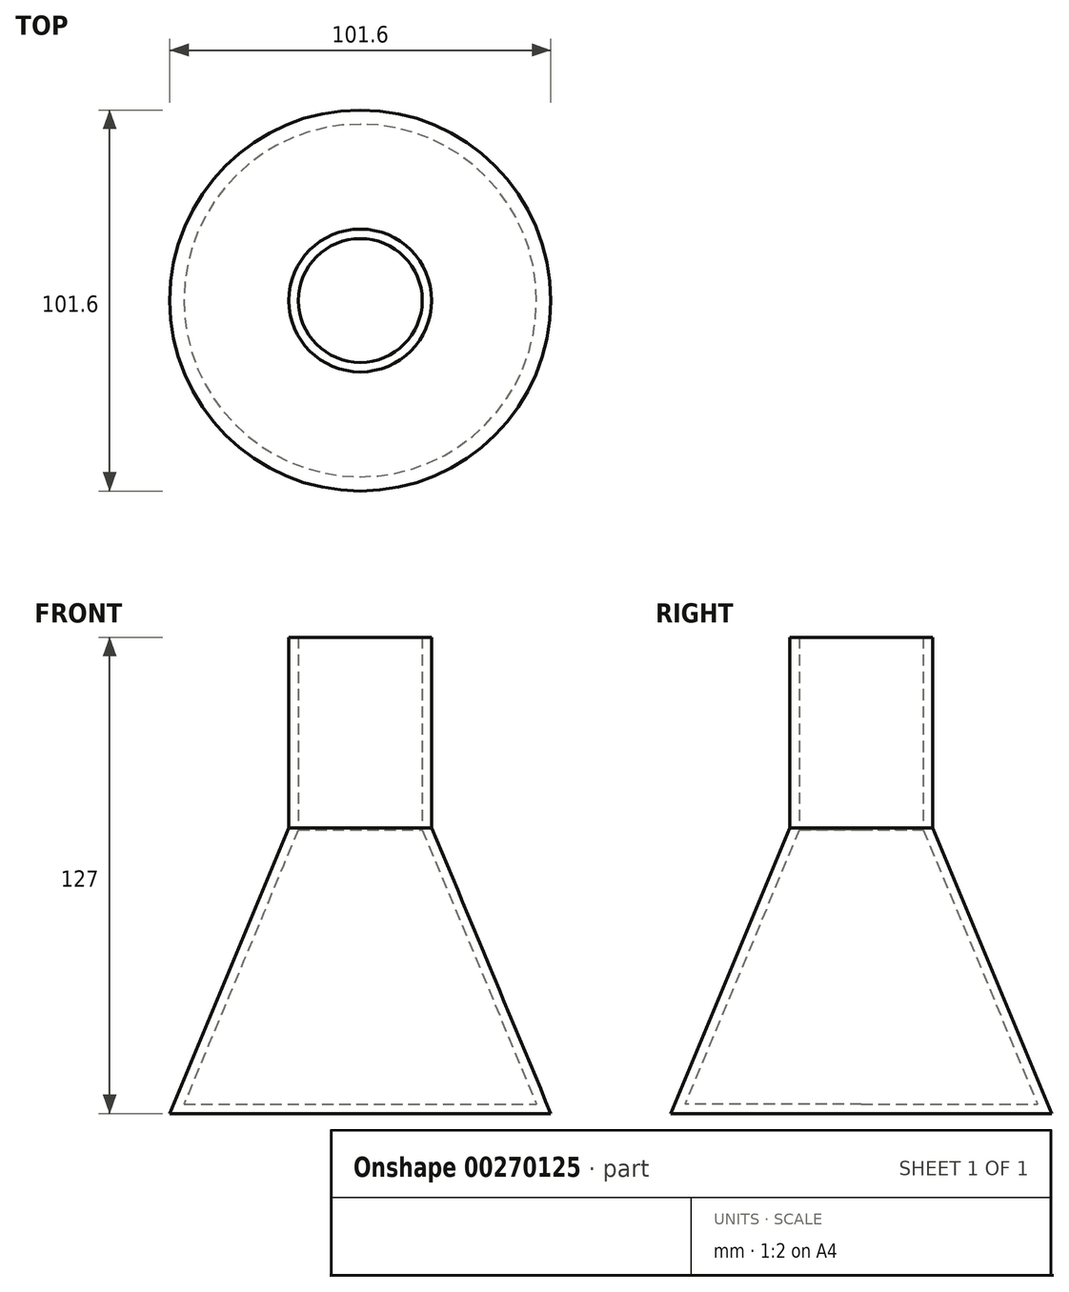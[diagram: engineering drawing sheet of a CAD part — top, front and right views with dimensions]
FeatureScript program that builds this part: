
annotation { "Feature Type Name" : "Feature", "Feature Type Description" : "" }
export const myFeature = defineFeature(function(context is Context, id is Id, definition is map)
    precondition{}
    {
        {
            var Q0;
            Q0=qCreatedBy(makeId("Top.planeOp"),FACE);
            var sketch = newSketch(context, id + "F0", { "sketchPlane" : qUnion([Q0])});
            skCircle(sketch, "E0", {"center": v(0, 0) * mm, "radius": 50.8 * mm});
            skSolve(sketch);
        }
        {
            var Q0;
            Q0=qCreatedBy(makeId("Top.planeOp"),FACE);
            cPlane(context, id + "F1", {"entities" : qUnion([Q0]), "cplaneType" : CPlaneType.OFFSET, "offset" : 76.2 * mm, "width" : 152.4 * mm, "height" : 152.4 * mm});
        }
        {
            var Q0;
            Q0=qCreatedBy(id+"F1.planeOp",FACE);
            var sketch = newSketch(context, id + "F2", { "sketchPlane" : qUnion([Q0])});
            skCircle(sketch, "E1", {"center": v(0, 0) * mm, "radius": 19.05 * mm});
            skSolve(sketch);
        }
        {
            var Q0;
            Q0=makeQuery(id+"F0.imprint","IMPRINT",FACE,{"disambiguationData":[TD([[makeQuery(id+"F0.imprint","IMPRINT",EDGE,{"derivedFrom":sQuery(id+"F0.wireOp",EDGE,"E0")}),1.0]])]});
            var Q1;
            Q1=makeQuery(id+"F2.imprint","IMPRINT",FACE,{"disambiguationData":[TD([[makeQuery(id+"F2.imprint","IMPRINT",EDGE,{"derivedFrom":sQuery(id+"F2.wireOp",EDGE,"E1")}),1.0]])]});
            loft(context, id + "F3", {"sheetProfilesArray" : [{ "sheetProfileEntities" : qUnion([Q0]) }, { "sheetProfileEntities" : qUnion([Q1]) }]});
        }
        {
            var Q0;
            Q0=makeQuery(id+"F3.opLoft","CAP_FACE",FACE,{"disambiguationData":[OSD([makeQuery(id+"F2.imprint","IMPRINT",FACE,{"disambiguationData":[TD([[makeQuery(id+"F2.imprint","IMPRINT",EDGE,{"derivedFrom":sQuery(id+"F2.wireOp",EDGE,"E1")}),1.0]])]})])],"isStart":true});
            var sketch = newSketch(context, id + "F4", { "sketchPlane" : qUnion([Q0])});
            skCircle(sketch, "E2", {"center": v(0, 0) * mm, "radius": 19.05 * mm});
            skSolve(sketch);
        }
        {
            var Q0;
            Q0=makeQuery(id+"F4.imprint","IMPRINT",FACE,{"disambiguationData":[TD([[makeQuery(id+"F4.imprint","IMPRINT",EDGE,{"derivedFrom":sQuery(id+"F4.wireOp",EDGE,"E2")}),1.0]])]});
            extrude(context, id + "F5", {"entities" : qUnion([Q0]), "operationType" : NewBodyOperationType.ADD, "depth" : 50.8 * mm});
        }
        {
            var Q0;
            Q0=makeQuery(id+"F5.opExtrude","CAP_FACE",FACE,{"disambiguationData":[OSD([sQuery(id+"F4.wireOp",EDGE,"E2")])],"isStart":false});
            shell(context, id + "F6", {"entities" : qUnion([Q0]), "thickness" : 2.54 * mm});
        }
    });
